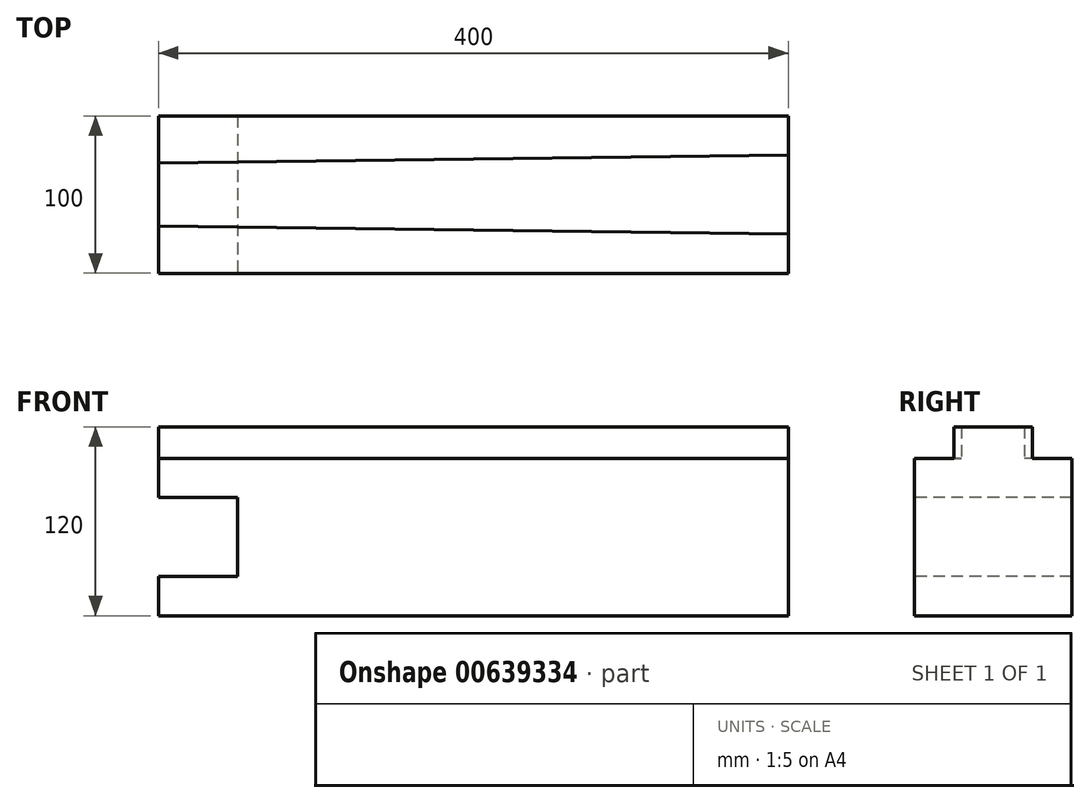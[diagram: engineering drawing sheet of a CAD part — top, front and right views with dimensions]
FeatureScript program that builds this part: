
annotation { "Feature Type Name" : "Feature", "Feature Type Description" : "" }
export const myFeature = defineFeature(function(context is Context, id is Id, definition is map)
    precondition{}
    {
        {
            var Q0;
            Q0=qCreatedBy(makeId("Top.planeOp"),FACE);
            var sketch = newSketch(context, id + "F0", { "sketchPlane" : qUnion([Q0])});
            skLineSegment(sketch, "E0.bottom", {"start": v(-129.43, 58.73) * mm, "end": v(270.57, 58.73) * mm});
            skLineSegment(sketch, "E0.top", {"start": v(-129.43, -41.27) * mm, "end": v(270.57, -41.27) * mm});
            skLineSegment(sketch, "E0.left", {"start": v(-129.43, 58.73) * mm, "end": v(-129.43, -41.27) * mm});
            skLineSegment(sketch, "E0.right", {"start": v(270.57, 58.73) * mm, "end": v(270.57, -41.27) * mm});
            skSolve(sketch);
        }
        {
            var Q0;
            Q0 = qSketchRegion(id + "F0", true);
            extrude(context, id + "F1", {"entities" : qUnion([Q0]), "depth" : 100 * mm, "offsetDistance" : 25 * mm});
        }
        {
            var Q0;
            Q0=makeQuery(id+"F1.opExtrude","CAP_FACE",FACE,{"disambiguationData":[OSD([sQuery(id+"F0.wireOp",EDGE,"E0.bottom"),sQuery(id+"F0.wireOp",EDGE,"E0.top"),sQuery(id+"F0.wireOp",EDGE,"E0.left"),sQuery(id+"F0.wireOp",EDGE,"E0.right")])],"isStart":false});
            var sketch = newSketch(context, id + "F2", { "sketchPlane" : qUnion([Q0])});
            skLineSegment(sketch, "E1.right", {"start": v(270.57, 33.73) * mm, "end": v(270.57, -16.27) * mm});
            skLineSegment(sketch, "E2", {"start": v(-129.43, 28.73) * mm, "end": v(-129.43, -11.27) * mm});
            skLineSegment(sketch, "E3", {"start": v(270.57, 33.73) * mm, "end": v(-129.43, 28.73) * mm});
            skLineSegment(sketch, "E4", {"start": v(270.57, -16.27) * mm, "end": v(-129.43, -11.27) * mm});
            skSolve(sketch);
        }
        {
            var Q0;
            Q0 = qSketchRegion(id + "F2", true);
            extrude(context, id + "F3", {"entities" : qUnion([Q0]), "operationType" : NewBodyOperationType.ADD, "depth" : 20 * mm, "offsetDistance" : 25 * mm});
        }
        {
            var Q0;
            Q0=makeQuery(id+"F3.boolean.opBoolean","MERGE",FACE,{"derivedFrom":[makeQuery(id+"F1.opExtrude","SWEPT_FACE",FACE,{"disambiguationData":[OSD([sQuery(id+"F0.wireOp",EDGE,"E0.left")])]}),makeQuery(id+"F3.opExtrude","SWEPT_FACE",FACE,{"disambiguationData":[OSD([sQuery(id+"F2.wireOp",EDGE,"E1.left")])]})]});
            var sketch = newSketch(context, id + "F4", { "sketchPlane" : qUnion([Q0])});
            skLineSegment(sketch, "E5.bottom", {"start": v(-58.73, 75) * mm, "end": v(41.27, 75) * mm});
            skLineSegment(sketch, "E5.top", {"start": v(-58.73, 25) * mm, "end": v(41.27, 25) * mm});
            skLineSegment(sketch, "E5.left", {"start": v(-58.73, 75) * mm, "end": v(-58.73, 25) * mm});
            skLineSegment(sketch, "E5.right", {"start": v(41.27, 75) * mm, "end": v(41.27, 25) * mm});
            skSolve(sketch);
        }
        {
            var Q0;
            Q0 = qSketchRegion(id + "F4", true);
            extrude(context, id + "F5", {"entities" : qUnion([Q0]), "operationType" : NewBodyOperationType.REMOVE, "oppositeDirection" : true, "depth" : 50 * mm, "offsetDistance" : 25 * mm});
        }
    });
